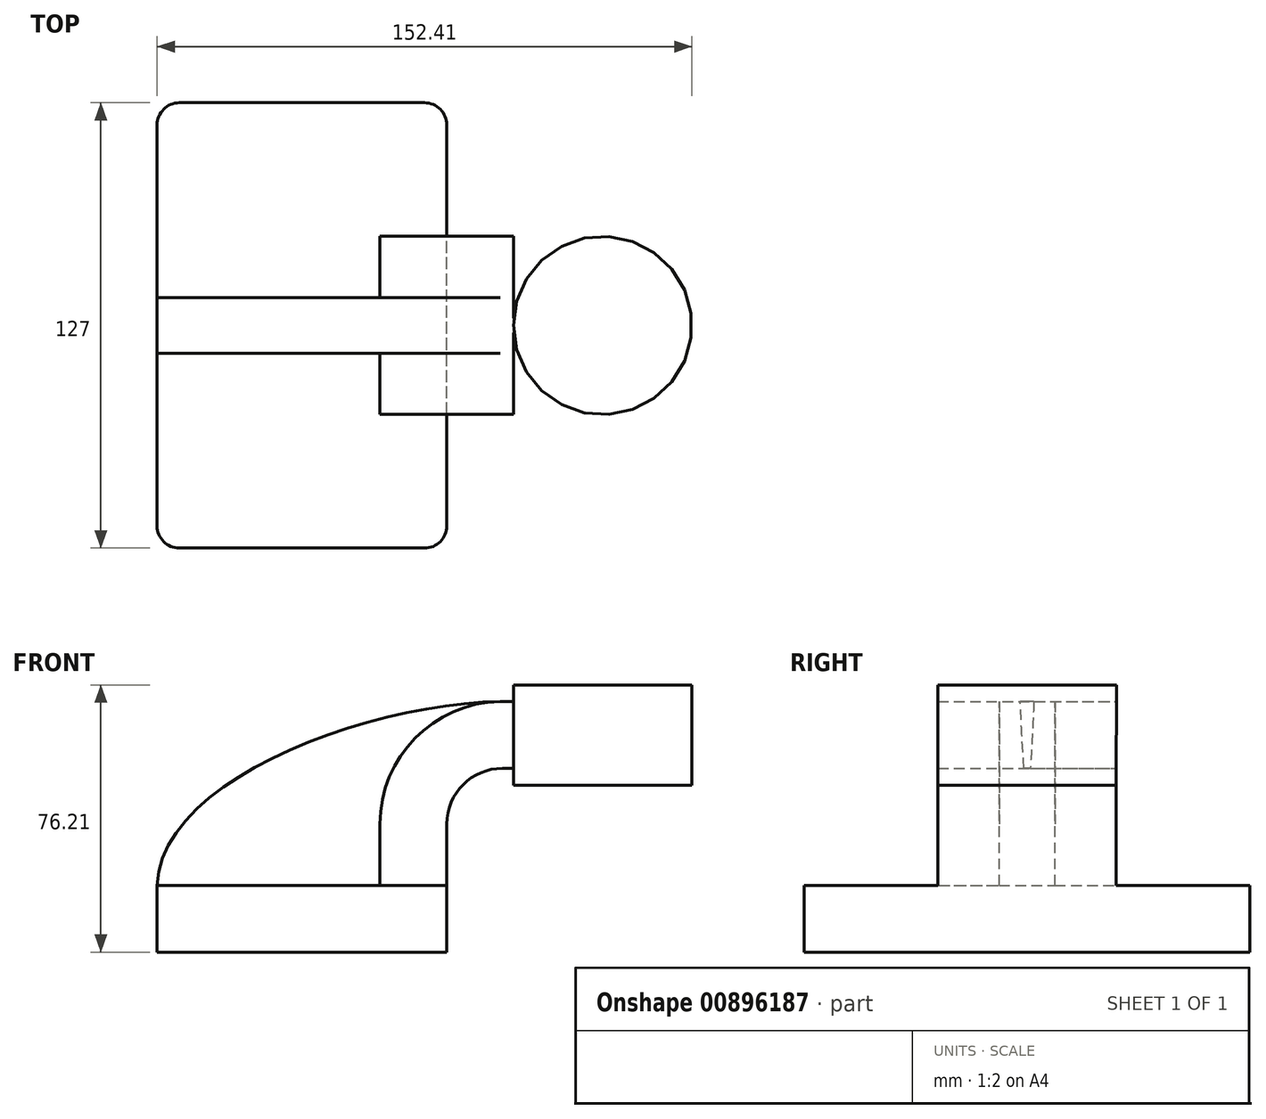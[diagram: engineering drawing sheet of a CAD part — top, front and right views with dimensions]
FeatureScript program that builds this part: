
annotation { "Feature Type Name" : "Feature", "Feature Type Description" : "" }
export const myFeature = defineFeature(function(context is Context, id is Id, definition is map)
    precondition{}
    {
        {
            var Q0;
            Q0=qCreatedBy(makeId("Front.planeOp"),FACE);
            var sketch = newSketch(context, id + "F0", { "sketchPlane" : qUnion([Q0])});
            skLineSegment(sketch, "E0.bottom", {"start": v(-41.28, -9.53) * mm, "end": v(41.28, -9.53) * mm});
            skLineSegment(sketch, "E0.top", {"start": v(-41.28, 9.52) * mm, "end": v(41.28, 9.52) * mm});
            skLineSegment(sketch, "E0.left", {"start": v(-41.28, -9.53) * mm, "end": v(-41.28, 9.53) * mm});
            skLineSegment(sketch, "E0.right", {"start": v(41.28, -9.53) * mm, "end": v(41.28, 9.52) * mm});
            skPoint(sketch, "E0.middle", {"position": v(0, 0) * mm});
            skLineSegment(sketch, "E1.bottom", {"start": v(111.12, 38.1) * mm, "end": v(60.32, 38.1) * mm});
            skLineSegment(sketch, "E1.top", {"start": v(111.12, 66.67) * mm, "end": v(60.32, 66.67) * mm});
            skLineSegment(sketch, "E1.left", {"start": v(111.12, 38.1) * mm, "end": v(111.12, 66.67) * mm});
            skLineSegment(sketch, "E1.right", {"start": v(60.32, 38.1) * mm, "end": v(60.32, 66.67) * mm});
            skPoint(sketch, "E1.middle", {"position": v(85.72, 52.39) * mm});
            skLineSegment(sketch, "E2", {"start": v(41.27, 9.52) * mm, "end": v(41.27, 27) * mm});
            skArc(sketch, "E3", {"start": v(41.28, 27) * mm, "mid": v(45.92, 38.23) * mm, "end": v(57.15, 42.88) * mm});
            skLineSegment(sketch, "E4", {"start": v(57.15, 42.88) * mm, "end": v(85.67, 42.88) * mm});
            skLineSegment(sketch, "E5.0", {"start": v(57.15, 61.93) * mm, "end": v(85.68, 61.93) * mm});
            skArc(sketch, "E5.1", {"start": v(22.23, 27) * mm, "mid": v(32.45, 51.7) * mm, "end": v(57.15, 61.93) * mm});
            skLineSegment(sketch, "E5.2", {"start": v(22.23, 9.52) * mm, "end": v(22.23, 27) * mm});
            skLineSegment(sketch, "E6", {"start": v(85.72, 38.1) * mm, "end": v(85.68, 66.67) * mm});
            skFitSpline(sketch, "E7", {"points": [v(-41.28, 9.53) * mm, v(57.15, 61.93) * mm], "startDerivative": vector(2.98, 91.5) * mm, "endDerivative": vector(111.72, 0.69) * mm});
            skLineSegment(sketch, "E8.bottom", {"start": v(60.32, 61.93) * mm, "end": v(85.67, 61.93) * mm});
            skLineSegment(sketch, "E8.top", {"start": v(60.32, 42.88) * mm, "end": v(85.67, 42.88) * mm});
            skLineSegment(sketch, "E8.left", {"start": v(60.32, 61.93) * mm, "end": v(60.32, 42.88) * mm});
            skLineSegment(sketch, "E8.right", {"start": v(85.67, 61.93) * mm, "end": v(85.67, 42.88) * mm});
            skSolve(sketch);
        }
        {
            var Q0;
            Q0=makeQuery(id+"F0.imprint","IMPRINT",FACE,{"disambiguationData":[TD([[makeQuery(id+"F0.imprint","IMPRINT",EDGE,{"derivedFrom":sQuery(id+"F0.wireOp",EDGE,"E0.bottom")}),1.0]])]});
            extrude(context, id + "F1", {"entities" : qUnion([Q0]), "endBound" : BoundingType.SYMMETRIC, "depth" : 127 * mm, "offsetDistance" : 25 * mm});
        }
        {
            var Q0;
            {var subQ1=sQuery(id+"F0.wireOp",EDGE,"E2");Q0=makeQuery(id+"F0.imprint","IMPRINT",FACE,{"disambiguationData":[TD([[makeQuery(id+"F0.imprint","IMPRINT",EDGE,{"derivedFrom":subQ1}),1.0]])]});}
            var Q1;
            Q1=makeQuery(id+"F0.imprint","IMPRINT",FACE,{"disambiguationData":[TD([[makeQuery(id+"F0.imprint","IMPRINT",EDGE,{"derivedFrom":sQuery(id+"F0.wireOp",EDGE,"E8.bottom")}),-1.0]])]});
            extrude(context, id + "F2", {"entities" : qUnion([Q0, Q1]), "operationType" : NewBodyOperationType.ADD, "endBound" : BoundingType.SYMMETRIC, "depth" : 50.8 * mm, "offsetDistance" : 25 * mm});
        }
        {
            var Q0;
            {var subQ3=sQuery(id+"F0.wireOp",EDGE,"E5.2");Q0=makeQuery(id+"F0.imprint","IMPRINT",FACE,{"disambiguationData":[TD([[makeQuery(id+"F0.imprint","IMPRINT",EDGE,{"derivedFrom":subQ3}),1.0]])]});}
            extrude(context, id + "F3", {"entities" : qUnion([Q0]), "operationType" : NewBodyOperationType.ADD, "endBound" : BoundingType.SYMMETRIC, "depth" : 15.88 * mm, "offsetDistance" : 25 * mm});
        }
        {
            var Q0;
            {var subQ0=sQuery(id+"F0.wireOp",EDGE,"E1.left");Q0=makeQuery(id+"F0.imprint","IMPRINT",FACE,{"disambiguationData":[TD([[makeQuery(id+"F0.imprint","IMPRINT",EDGE,{"derivedFrom":subQ0}),1.0]])]});}
            var Q1;
            Q1=sQuery(id+"F0.wireOp",EDGE,"E6");
            revolve(context, id + "F4", {"operationType" : NewBodyOperationType.ADD, "surfaceOperationType" : NewSurfaceOperationType.NEW, "entities" : qUnion([Q0]), "axis" : qUnion([Q1]), "revolveType" : RevolveType.FULL});
        }
        {
            var Q0;
            Q0=makeQuery(id+"F1.opExtrude","CAP_EDGE",EDGE,{"disambiguationData":[OSD([sQuery(id+"F0.wireOp",EDGE,"E0.right")])],"isStart":false});
            var Q1;
            Q1=makeQuery(id+"F1.opExtrude","CAP_EDGE",EDGE,{"disambiguationData":[OSD([sQuery(id+"F0.wireOp",EDGE,"E0.left")])],"isStart":false});
            var Q2;
            Q2=makeQuery(id+"F1.opExtrude","CAP_EDGE",EDGE,{"disambiguationData":[OSD([sQuery(id+"F0.wireOp",EDGE,"E0.right")])],"isStart":true});
            var Q3;
            Q3=makeQuery(id+"F1.opExtrude","CAP_EDGE",EDGE,{"disambiguationData":[OSD([sQuery(id+"F0.wireOp",EDGE,"E0.left")])],"isStart":true});
            fillet(context, id + "F5", {"entities" : qUnion([Q0, Q1, Q2, Q3]), "radius" : 6.35 * mm, "tangentPropagation" : true, "allowEdgeOverflow" : false});
        }
    });
